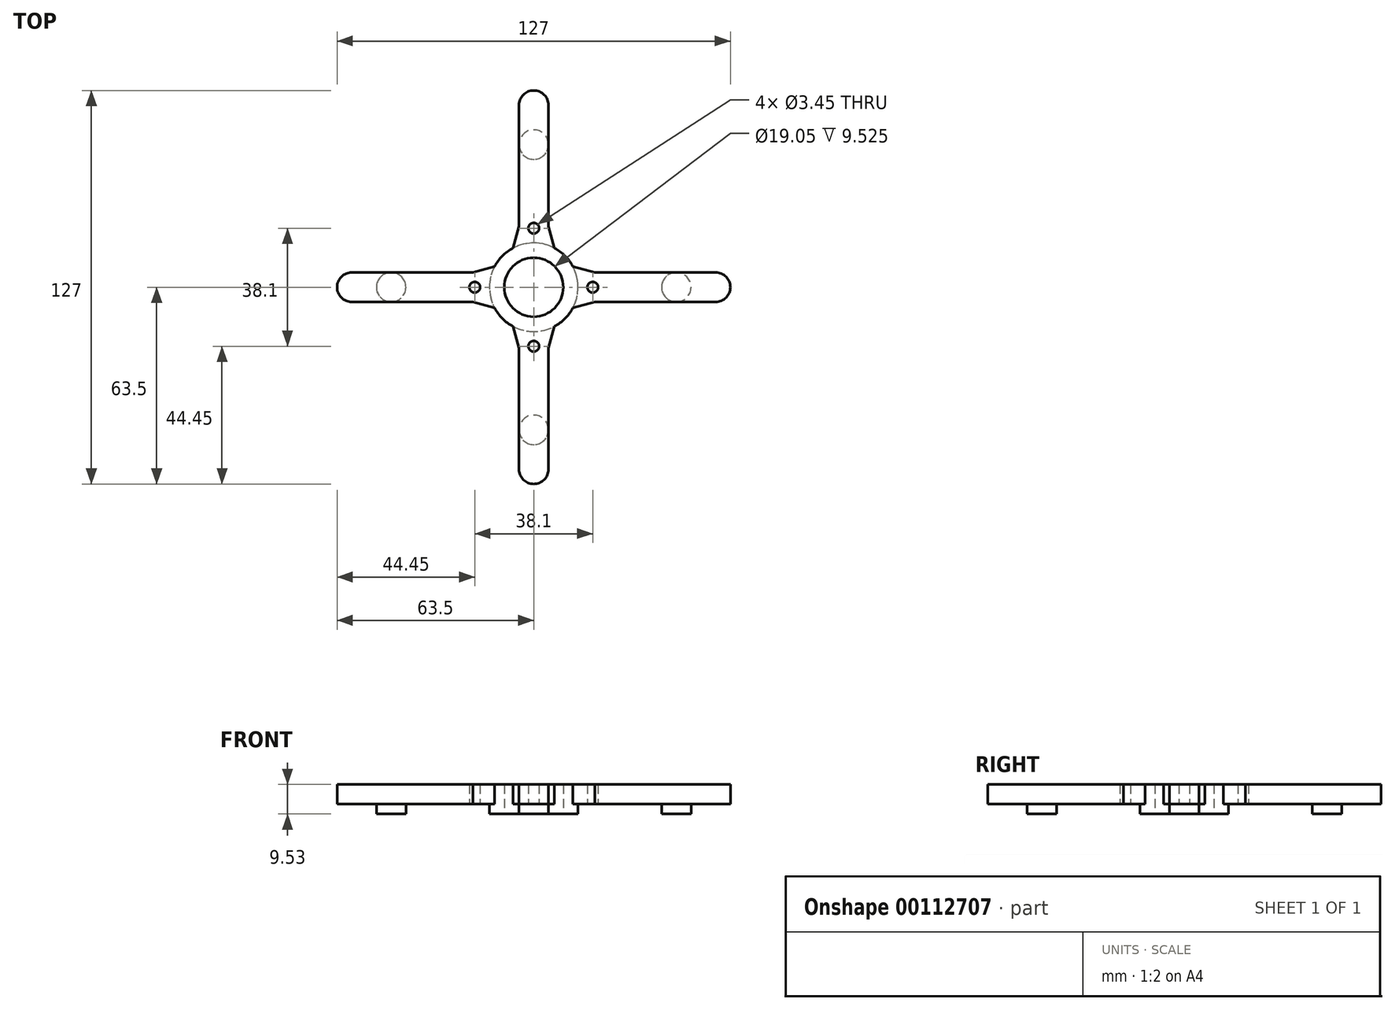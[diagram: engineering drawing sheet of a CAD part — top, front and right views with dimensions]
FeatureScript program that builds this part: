
annotation { "Feature Type Name" : "Feature", "Feature Type Description" : "" }
export const myFeature = defineFeature(function(context is Context, id is Id, definition is map)
    precondition{}
    {
        {
            var Q0;
            Q0=qCreatedBy(makeId("Top.planeOp"),FACE);
            var sketch = newSketch(context, id + "F0", { "sketchPlane" : qUnion([Q0])});
            skLineSegment(sketch, "E0", {"start": v(-19.05, 0) * mm, "end": v(19.05, 0) * mm, "construction": true});
            skLineSegment(sketch, "E1", {"start": v(0, 19.05) * mm, "end": v(0, -19.05) * mm, "construction": true});
            skCircle(sketch, "E2", {"center": v(-19.05, 0) * mm, "radius": 1.73 * mm});
            skCircle(sketch, "E3", {"center": v(0, 19.05) * mm, "radius": 1.73 * mm});
            skCircle(sketch, "E4", {"center": v(19.05, 0) * mm, "radius": 1.73 * mm});
            skCircle(sketch, "E5", {"center": v(0, -19.05) * mm, "radius": 1.73 * mm});
            skCircle(sketch, "E6", {"center": v(0, 0) * mm, "radius": 9.53 * mm});
            skLineSegment(sketch, "E7.bottom", {"start": v(4.76, 13.47) * mm, "end": v(-4.76, 13.47) * mm, "construction": true});
            skLineSegment(sketch, "E7.top", {"start": v(4.76, 63.5) * mm, "end": v(-4.76, 63.5) * mm});
            skLineSegment(sketch, "E7.left", {"start": v(4.76, 13.47) * mm, "end": v(4.76, 63.5) * mm});
            skLineSegment(sketch, "E7.right", {"start": v(-4.76, 13.47) * mm, "end": v(-4.76, 63.5) * mm});
            skArc(sketch, "E8", {"start": v(13.47, 4.76) * mm, "mid": v(10.1, 10.1) * mm, "end": v(4.76, 13.47) * mm});
            skLineSegment(sketch, "E9", {"start": v(0, 19.05) * mm, "end": v(0, 63.5) * mm, "construction": true});
            skLineSegment(sketch, "E10", {"start": v(-19.05, 0) * mm, "end": v(-63.5, 0) * mm, "construction": true});
            skLineSegment(sketch, "E11", {"start": v(0, -19.05) * mm, "end": v(0, -63.5) * mm, "construction": true});
            skLineSegment(sketch, "E12", {"start": v(19.05, 0) * mm, "end": v(63.5, 0) * mm, "construction": true});
            skLineSegment(sketch, "E13.bottom", {"start": v(-13.47, -4.76) * mm, "end": v(-63.5, -4.76) * mm});
            skLineSegment(sketch, "E13.top", {"start": v(-13.47, 4.76) * mm, "end": v(-63.5, 4.76) * mm});
            skLineSegment(sketch, "E13.left", {"start": v(-13.47, -4.76) * mm, "end": v(-13.47, 4.76) * mm, "construction": true});
            skLineSegment(sketch, "E13.right", {"start": v(-63.5, -4.76) * mm, "end": v(-63.5, 4.76) * mm});
            skLineSegment(sketch, "E14.bottom", {"start": v(13.47, -4.76) * mm, "end": v(63.5, -4.76) * mm});
            skLineSegment(sketch, "E14.top", {"start": v(13.47, 4.76) * mm, "end": v(63.5, 4.76) * mm});
            skLineSegment(sketch, "E14.left", {"start": v(13.47, -4.76) * mm, "end": v(13.47, 4.76) * mm, "construction": true});
            skLineSegment(sketch, "E14.right", {"start": v(63.5, -4.76) * mm, "end": v(63.5, 4.76) * mm});
            skLineSegment(sketch, "E15.bottom", {"start": v(4.76, -63.5) * mm, "end": v(-4.76, -63.5) * mm});
            skLineSegment(sketch, "E15.top", {"start": v(4.76, -13.47) * mm, "end": v(-4.76, -13.47) * mm, "construction": true});
            skLineSegment(sketch, "E15.left", {"start": v(4.76, -63.5) * mm, "end": v(4.76, -13.47) * mm});
            skLineSegment(sketch, "E15.right", {"start": v(-4.76, -63.5) * mm, "end": v(-4.76, -13.47) * mm});
            skArc(sketch, "E16", {"start": v(-4.76, 13.47) * mm, "mid": v(-10.1, 10.1) * mm, "end": v(-13.47, 4.76) * mm});
            skArc(sketch, "E17", {"start": v(-13.47, -4.76) * mm, "mid": v(-10.1, -10.1) * mm, "end": v(-4.76, -13.47) * mm});
            skArc(sketch, "E18", {"start": v(4.76, -13.47) * mm, "mid": v(10.1, -10.1) * mm, "end": v(13.47, -4.76) * mm});
            skSolve(sketch);
        }
        {
            var Q0;
            Q0=makeQuery(id+"F0.imprint","IMPRINT",FACE,{"disambiguationData":[TD([[makeQuery(id+"F0.imprint","IMPRINT",EDGE,{"derivedFrom":sQuery(id+"F0.wireOp",EDGE,"E2")}),-1.0]])]});
            extrude(context, id + "F1", {"entities" : qUnion([Q0]), "depth" : 6.35 * mm});
        }
        {
            var Q0;
            Q0=makeQuery(id+"F1.opExtrude","CAP_FACE",FACE,{"disambiguationData":[OSD([sQuery(id+"F0.wireOp",EDGE,"E2"),sQuery(id+"F0.wireOp",EDGE,"E3"),sQuery(id+"F0.wireOp",EDGE,"E4"),sQuery(id+"F0.wireOp",EDGE,"E5"),sQuery(id+"F0.wireOp",EDGE,"E6"),sQuery(id+"F0.wireOp",EDGE,"E7.top"),sQuery(id+"F0.wireOp",EDGE,"E7.left"),sQuery(id+"F0.wireOp",EDGE,"E7.right"),sQuery(id+"F0.wireOp",EDGE,"E8"),sQuery(id+"F0.wireOp",EDGE,"E13.bottom"),sQuery(id+"F0.wireOp",EDGE,"E13.top"),sQuery(id+"F0.wireOp",EDGE,"E13.right"),sQuery(id+"F0.wireOp",EDGE,"E14.bottom"),sQuery(id+"F0.wireOp",EDGE,"E14.top"),sQuery(id+"F0.wireOp",EDGE,"E14.right"),sQuery(id+"F0.wireOp",EDGE,"E15.bottom"),sQuery(id+"F0.wireOp",EDGE,"E15.left"),sQuery(id+"F0.wireOp",EDGE,"E15.right"),sQuery(id+"F0.wireOp",EDGE,"E16"),sQuery(id+"F0.wireOp",EDGE,"E17"),sQuery(id+"F0.wireOp",EDGE,"E18")])],"isStart":true});
            var sketch = newSketch(context, id + "F2", { "sketchPlane" : qUnion([Q0])});
            skLineSegment(sketch, "E19.bottom", {"start": v(-50.8, 4.76) * mm, "end": v(-41.28, 4.76) * mm});
            skLineSegment(sketch, "E19.top", {"start": v(-50.8, -4.76) * mm, "end": v(-41.28, -4.76) * mm});
            skLineSegment(sketch, "E19.left", {"start": v(-50.8, 4.76) * mm, "end": v(-50.8, -4.76) * mm});
            skLineSegment(sketch, "E19.right", {"start": v(-41.28, 4.76) * mm, "end": v(-41.28, -4.76) * mm});
            skLineSegment(sketch, "E20.bottom", {"start": v(-4.76, 50.8) * mm, "end": v(4.76, 50.8) * mm});
            skLineSegment(sketch, "E20.top", {"start": v(-4.76, 41.28) * mm, "end": v(4.76, 41.28) * mm});
            skLineSegment(sketch, "E20.left", {"start": v(-4.76, 50.8) * mm, "end": v(-4.76, 41.28) * mm});
            skLineSegment(sketch, "E20.right", {"start": v(4.76, 50.8) * mm, "end": v(4.76, 41.28) * mm});
            skLineSegment(sketch, "E21.bottom", {"start": v(50.8, -4.76) * mm, "end": v(41.27, -4.76) * mm});
            skLineSegment(sketch, "E21.top", {"start": v(50.8, 4.76) * mm, "end": v(41.27, 4.76) * mm});
            skLineSegment(sketch, "E21.left", {"start": v(50.8, -4.76) * mm, "end": v(50.8, 4.76) * mm});
            skLineSegment(sketch, "E21.right", {"start": v(41.27, -4.76) * mm, "end": v(41.27, 4.76) * mm});
            skLineSegment(sketch, "E22.bottom", {"start": v(4.76, -50.8) * mm, "end": v(-4.76, -50.8) * mm});
            skLineSegment(sketch, "E22.top", {"start": v(4.76, -41.27) * mm, "end": v(-4.76, -41.27) * mm});
            skLineSegment(sketch, "E22.left", {"start": v(4.76, -50.8) * mm, "end": v(4.76, -41.27) * mm});
            skLineSegment(sketch, "E22.right", {"start": v(-4.76, -50.8) * mm, "end": v(-4.76, -41.27) * mm});
            skCircle(sketch, "E23", {"center": v(0, 0) * mm, "radius": 9.53 * mm});
            skCircle(sketch, "E24", {"center": v(0, 0) * mm, "radius": 14.29 * mm});
            skSolve(sketch);
        }
        {
            var Q0;
            Q0 = qSketchRegion(id + "F2", true);
            extrude(context, id + "F3", {"entities" : qUnion([Q0]), "operationType" : NewBodyOperationType.ADD, "depth" : 3.17 * mm});
        }
        {
            var Q0;
            Q0=makeQuery(id+"F3.opExtrude","SWEPT_EDGE",EDGE,{"disambiguationData":[OSD([sQuery(id+"F0.wireOp",EDGE,"E15.left"),sQuery(id+"F2.wireOp",EDGE,"E20.top"),sQuery(id+"F2.wireOp",EDGE,"E20.right")])]});
            var Q1;
            Q1=makeQuery(id+"F3.boolean.opBoolean","MERGE",EDGE,{"derivedFrom":[makeQuery(id+"F1.opExtrude","SWEPT_EDGE",EDGE,{"disambiguationData":[OSD([sQuery(id+"F0.wireOp",EDGE,"E15.bottom"),sQuery(id+"F0.wireOp",EDGE,"E15.left")])]}),makeQuery(id+"F3.opExtrude","SWEPT_EDGE",EDGE,{"disambiguationData":[OSD([sQuery(id+"F2.wireOp",EDGE,"E20.bottom"),sQuery(id+"F2.wireOp",EDGE,"E20.right")])]})]});
            var Q2;
            Q2=makeQuery(id+"F3.opExtrude","SWEPT_EDGE",EDGE,{"disambiguationData":[OSD([sQuery(id+"F0.wireOp",EDGE,"E15.right"),sQuery(id+"F2.wireOp",EDGE,"E20.top"),sQuery(id+"F2.wireOp",EDGE,"E20.left")])]});
            var Q3;
            Q3=makeQuery(id+"F3.boolean.opBoolean","MERGE",EDGE,{"derivedFrom":[makeQuery(id+"F1.opExtrude","SWEPT_EDGE",EDGE,{"disambiguationData":[OSD([sQuery(id+"F0.wireOp",EDGE,"E14.top"),sQuery(id+"F0.wireOp",EDGE,"E14.right")])]}),makeQuery(id+"F3.opExtrude","SWEPT_EDGE",EDGE,{"disambiguationData":[OSD([sQuery(id+"F2.wireOp",EDGE,"E21.bottom"),sQuery(id+"F2.wireOp",EDGE,"E21.left")])]})]});
            var Q4;
            Q4=makeQuery(id+"F3.boolean.opBoolean","MERGE",EDGE,{"derivedFrom":[makeQuery(id+"F1.opExtrude","SWEPT_EDGE",EDGE,{"disambiguationData":[OSD([sQuery(id+"F0.wireOp",EDGE,"E14.bottom"),sQuery(id+"F0.wireOp",EDGE,"E14.right")])]}),makeQuery(id+"F3.opExtrude","SWEPT_EDGE",EDGE,{"disambiguationData":[OSD([sQuery(id+"F2.wireOp",EDGE,"E21.top"),sQuery(id+"F2.wireOp",EDGE,"E21.left")])]})]});
            var Q5;
            Q5=makeQuery(id+"F3.boolean.opBoolean","MERGE",EDGE,{"derivedFrom":[makeQuery(id+"F1.opExtrude","SWEPT_EDGE",EDGE,{"disambiguationData":[OSD([sQuery(id+"F0.wireOp",EDGE,"E15.bottom"),sQuery(id+"F0.wireOp",EDGE,"E15.right")])]}),makeQuery(id+"F3.opExtrude","SWEPT_EDGE",EDGE,{"disambiguationData":[OSD([sQuery(id+"F2.wireOp",EDGE,"E20.bottom"),sQuery(id+"F2.wireOp",EDGE,"E20.left")])]})]});
            var Q6;
            Q6=makeQuery(id+"F3.opExtrude","SWEPT_EDGE",EDGE,{"disambiguationData":[OSD([sQuery(id+"F0.wireOp",EDGE,"E14.bottom"),sQuery(id+"F2.wireOp",EDGE,"E21.top"),sQuery(id+"F2.wireOp",EDGE,"E21.right")])]});
            var Q7;
            Q7=makeQuery(id+"F3.opExtrude","SWEPT_EDGE",EDGE,{"disambiguationData":[OSD([sQuery(id+"F0.wireOp",EDGE,"E14.top"),sQuery(id+"F2.wireOp",EDGE,"E21.bottom"),sQuery(id+"F2.wireOp",EDGE,"E21.right")])]});
            var Q8;
            Q8=makeQuery(id+"F3.opExtrude","SWEPT_EDGE",EDGE,{"disambiguationData":[OSD([sQuery(id+"F0.wireOp",EDGE,"E13.bottom"),sQuery(id+"F2.wireOp",EDGE,"E19.bottom"),sQuery(id+"F2.wireOp",EDGE,"E19.right")])]});
            var Q9;
            Q9=makeQuery(id+"F3.boolean.opBoolean","MERGE",EDGE,{"derivedFrom":[makeQuery(id+"F1.opExtrude","SWEPT_EDGE",EDGE,{"disambiguationData":[OSD([sQuery(id+"F0.wireOp",EDGE,"E13.bottom"),sQuery(id+"F0.wireOp",EDGE,"E13.right")])]}),makeQuery(id+"F3.opExtrude","SWEPT_EDGE",EDGE,{"disambiguationData":[OSD([sQuery(id+"F2.wireOp",EDGE,"E19.bottom"),sQuery(id+"F2.wireOp",EDGE,"E19.left")])]})]});
            var Q10;
            Q10=makeQuery(id+"F3.boolean.opBoolean","MERGE",EDGE,{"derivedFrom":[makeQuery(id+"F1.opExtrude","SWEPT_EDGE",EDGE,{"disambiguationData":[OSD([sQuery(id+"F0.wireOp",EDGE,"E13.top"),sQuery(id+"F0.wireOp",EDGE,"E13.right")])]}),makeQuery(id+"F3.opExtrude","SWEPT_EDGE",EDGE,{"disambiguationData":[OSD([sQuery(id+"F2.wireOp",EDGE,"E19.top"),sQuery(id+"F2.wireOp",EDGE,"E19.left")])]})]});
            var Q11;
            Q11=makeQuery(id+"F3.opExtrude","SWEPT_EDGE",EDGE,{"disambiguationData":[OSD([sQuery(id+"F0.wireOp",EDGE,"E13.top"),sQuery(id+"F2.wireOp",EDGE,"E19.top"),sQuery(id+"F2.wireOp",EDGE,"E19.right")])]});
            var Q12;
            Q12=makeQuery(id+"F3.opExtrude","SWEPT_EDGE",EDGE,{"disambiguationData":[OSD([sQuery(id+"F0.wireOp",EDGE,"E7.left"),sQuery(id+"F2.wireOp",EDGE,"E22.top"),sQuery(id+"F2.wireOp",EDGE,"E22.left")])]});
            var Q13;
            Q13=makeQuery(id+"F3.boolean.opBoolean","MERGE",EDGE,{"derivedFrom":[makeQuery(id+"F1.opExtrude","SWEPT_EDGE",EDGE,{"disambiguationData":[OSD([sQuery(id+"F0.wireOp",EDGE,"E7.top"),sQuery(id+"F0.wireOp",EDGE,"E7.left")])]}),makeQuery(id+"F3.opExtrude","SWEPT_EDGE",EDGE,{"disambiguationData":[OSD([sQuery(id+"F2.wireOp",EDGE,"E22.bottom"),sQuery(id+"F2.wireOp",EDGE,"E22.left")])]})]});
            var Q14;
            Q14=makeQuery(id+"F3.boolean.opBoolean","MERGE",EDGE,{"derivedFrom":[makeQuery(id+"F1.opExtrude","SWEPT_EDGE",EDGE,{"disambiguationData":[OSD([sQuery(id+"F0.wireOp",EDGE,"E7.top"),sQuery(id+"F0.wireOp",EDGE,"E7.right")])]}),makeQuery(id+"F3.opExtrude","SWEPT_EDGE",EDGE,{"disambiguationData":[OSD([sQuery(id+"F2.wireOp",EDGE,"E22.bottom"),sQuery(id+"F2.wireOp",EDGE,"E22.right")])]})]});
            var Q15;
            Q15=makeQuery(id+"F3.opExtrude","SWEPT_EDGE",EDGE,{"disambiguationData":[OSD([sQuery(id+"F0.wireOp",EDGE,"E7.right"),sQuery(id+"F2.wireOp",EDGE,"E22.top"),sQuery(id+"F2.wireOp",EDGE,"E22.right")])]});
            fillet(context, id + "F4", {"entities" : qUnion([Q0, Q1, Q2, Q3, Q4, Q5, Q6, Q7, Q8, Q9, Q10, Q11, Q12, Q13, Q14, Q15]), "radius" : 4.76 * mm, "tangentPropagation" : true, "allowEdgeOverflow" : false});
        }
        {
            var Q0;
            Q0=makeQuery(id+"F1.opExtrude","CAP_FACE",FACE,{"disambiguationData":[OSD([sQuery(id+"F0.wireOp",EDGE,"E2"),sQuery(id+"F0.wireOp",EDGE,"E3"),sQuery(id+"F0.wireOp",EDGE,"E4"),sQuery(id+"F0.wireOp",EDGE,"E5"),sQuery(id+"F0.wireOp",EDGE,"E6"),sQuery(id+"F0.wireOp",EDGE,"E7.top"),sQuery(id+"F0.wireOp",EDGE,"E7.left"),sQuery(id+"F0.wireOp",EDGE,"E7.right"),sQuery(id+"F0.wireOp",EDGE,"E8"),sQuery(id+"F0.wireOp",EDGE,"E13.bottom"),sQuery(id+"F0.wireOp",EDGE,"E13.top"),sQuery(id+"F0.wireOp",EDGE,"E13.right"),sQuery(id+"F0.wireOp",EDGE,"E14.bottom"),sQuery(id+"F0.wireOp",EDGE,"E14.top"),sQuery(id+"F0.wireOp",EDGE,"E14.right"),sQuery(id+"F0.wireOp",EDGE,"E15.bottom"),sQuery(id+"F0.wireOp",EDGE,"E15.left"),sQuery(id+"F0.wireOp",EDGE,"E15.right"),sQuery(id+"F0.wireOp",EDGE,"E16"),sQuery(id+"F0.wireOp",EDGE,"E17"),sQuery(id+"F0.wireOp",EDGE,"E18")])],"isStart":false});
            var sketch = newSketch(context, id + "F5", { "sketchPlane" : qUnion([Q0])});
            skLineSegment(sketch, "E25", {"start": v(-19.68, 4.76) * mm, "end": v(-12.65, 6.65) * mm});
            skLineSegment(sketch, "E26", {"start": v(-19.68, 4.76) * mm, "end": v(-20.28, 4.6) * mm, "construction": true});
            skArc(sketch, "E27", {"start": v(-20.28, 4.6) * mm, "mid": v(-23.81, 0) * mm, "end": v(-20.28, -4.6) * mm, "construction": true});
            skLineSegment(sketch, "E28", {"start": v(-19.68, 4.76) * mm, "end": v(-13.47, 4.76) * mm});
            skArc(sketch, "E29", {"start": v(-12.65, 6.65) * mm, "mid": v(-13.1, 5.72) * mm, "end": v(-13.47, 4.76) * mm});
            skLineSegment(sketch, "E30", {"start": v(-4.76, 13.47) * mm, "end": v(-4.76, 19.68) * mm});
            skLineSegment(sketch, "E31", {"start": v(4.76, 13.47) * mm, "end": v(4.76, 19.68) * mm});
            skLineSegment(sketch, "E32", {"start": v(13.47, 4.76) * mm, "end": v(19.68, 4.76) * mm});
            skLineSegment(sketch, "E33", {"start": v(13.47, -4.76) * mm, "end": v(19.68, -4.76) * mm});
            skLineSegment(sketch, "E34", {"start": v(4.76, -13.47) * mm, "end": v(4.76, -19.68) * mm});
            skLineSegment(sketch, "E35", {"start": v(-4.76, -13.47) * mm, "end": v(-4.76, -19.68) * mm});
            skLineSegment(sketch, "E36", {"start": v(-4.76, -19.68) * mm, "end": v(-6.65, -12.65) * mm});
            skLineSegment(sketch, "E37", {"start": v(4.76, -19.68) * mm, "end": v(6.65, -12.65) * mm});
            skLineSegment(sketch, "E38", {"start": v(19.68, -4.76) * mm, "end": v(12.65, -6.65) * mm});
            skLineSegment(sketch, "E39", {"start": v(19.68, 4.76) * mm, "end": v(12.65, 6.65) * mm});
            skLineSegment(sketch, "E40", {"start": v(4.76, 19.68) * mm, "end": v(6.65, 12.65) * mm});
            skLineSegment(sketch, "E41", {"start": v(-4.76, 19.68) * mm, "end": v(-6.65, 12.65) * mm});
            skArc(sketch, "E42", {"start": v(-4.76, 13.47) * mm, "mid": v(-5.72, 13.1) * mm, "end": v(-6.65, 12.65) * mm});
            skArc(sketch, "E43", {"start": v(6.65, 12.65) * mm, "mid": v(5.72, 13.1) * mm, "end": v(4.76, 13.47) * mm});
            skArc(sketch, "E44", {"start": v(13.47, 4.76) * mm, "mid": v(13.1, 5.72) * mm, "end": v(12.65, 6.65) * mm});
            skLineSegment(sketch, "E45", {"start": v(-20.28, -4.6) * mm, "end": v(-19.68, -4.76) * mm, "construction": true});
            skLineSegment(sketch, "E46", {"start": v(-19.68, -4.76) * mm, "end": v(-12.65, -6.65) * mm});
            skLineSegment(sketch, "E47", {"start": v(-13.47, -4.76) * mm, "end": v(-19.68, -4.76) * mm});
            skArc(sketch, "E48", {"start": v(-13.47, -4.76) * mm, "mid": v(-13.1, -5.72) * mm, "end": v(-12.65, -6.65) * mm});
            skArc(sketch, "E49", {"start": v(-6.65, -12.65) * mm, "mid": v(-5.72, -13.1) * mm, "end": v(-4.76, -13.47) * mm});
            skArc(sketch, "E50", {"start": v(4.76, -13.47) * mm, "mid": v(5.72, -13.1) * mm, "end": v(6.65, -12.65) * mm});
            skArc(sketch, "E51", {"start": v(12.65, -6.65) * mm, "mid": v(13.1, -5.72) * mm, "end": v(13.47, -4.76) * mm});
            skSolve(sketch);
        }
        {
            var Q0;
            Q0 = qSketchRegion(id + "F5", true);
            var Q1;
            {var subQ0=sQuery(id+"F0.wireOp",EDGE,"E18");var subQ1=sQuery(id+"F0.wireOp",EDGE,"E17");var subQ2=sQuery(id+"F0.wireOp",EDGE,"E16");var subQ3=sQuery(id+"F0.wireOp",EDGE,"E2");var subQ4=sQuery(id+"F0.wireOp",EDGE,"E8");var subQ5=sQuery(id+"F0.wireOp",EDGE,"E13.bottom");var subQ6=sQuery(id+"F0.wireOp",EDGE,"E13.top");Q1=makeQuery(id+"F3.boolean.opBoolean","SPLIT",FACE,{"disambiguationData":[TD([makeQuery(id+"F1.opExtrude","SWEPT_FACE",FACE,{"disambiguationData":[OSD([subQ3])]})])],"derivedFrom":makeQuery(id+"F1.opExtrude","CAP_FACE",FACE,{"disambiguationData":[OSD([subQ3,sQuery(id+"F0.wireOp",EDGE,"E3"),sQuery(id+"F0.wireOp",EDGE,"E4"),sQuery(id+"F0.wireOp",EDGE,"E5"),sQuery(id+"F0.wireOp",EDGE,"E6"),sQuery(id+"F0.wireOp",EDGE,"E7.top"),sQuery(id+"F0.wireOp",EDGE,"E7.left"),sQuery(id+"F0.wireOp",EDGE,"E7.right"),subQ4,subQ5,subQ6,sQuery(id+"F0.wireOp",EDGE,"E13.right"),sQuery(id+"F0.wireOp",EDGE,"E14.bottom"),sQuery(id+"F0.wireOp",EDGE,"E14.top"),sQuery(id+"F0.wireOp",EDGE,"E14.right"),sQuery(id+"F0.wireOp",EDGE,"E15.bottom"),sQuery(id+"F0.wireOp",EDGE,"E15.left"),sQuery(id+"F0.wireOp",EDGE,"E15.right"),subQ2,subQ1,subQ0])],"isStart":true})});}
            extrude(context, id + "F6", {"entities" : qUnion([Q0]), "operationType" : NewBodyOperationType.ADD, "endBound" : BoundingType.UP_TO_SURFACE, "oppositeDirection" : true, "endBoundEntityFace" : qUnion([Q1]), "depth" : 25.4 * mm});
        }
    });
